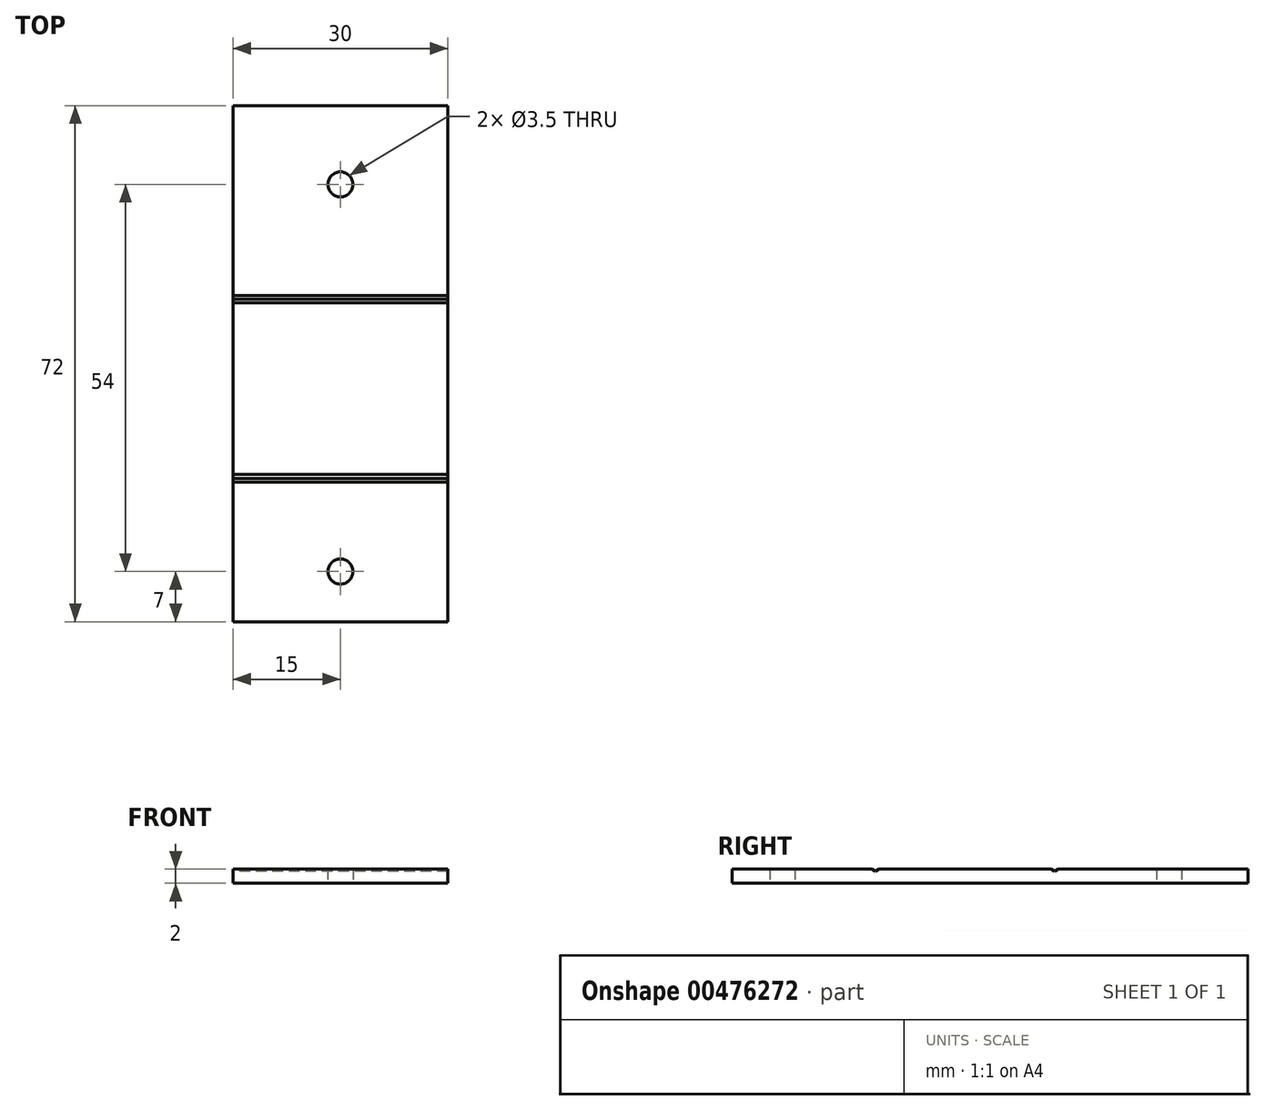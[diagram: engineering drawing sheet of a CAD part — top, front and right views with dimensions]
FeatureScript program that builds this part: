
annotation { "Feature Type Name" : "Feature", "Feature Type Description" : "" }
export const myFeature = defineFeature(function(context is Context, id is Id, definition is map)
    precondition{}
    {
        {
            var Q0;
            Q0=qCreatedBy(makeId("Top.planeOp"),FACE);
            var sketch = newSketch(context, id + "F0", { "sketchPlane" : qUnion([Q0])});
            skLineSegment(sketch, "E0.bottom", {"start": v(0, 0) * mm, "end": v(30, 0) * mm});
            skLineSegment(sketch, "E0.top", {"start": v(0, 72) * mm, "end": v(30, 72) * mm});
            skLineSegment(sketch, "E0.left", {"start": v(0, 0) * mm, "end": v(0, 72) * mm});
            skLineSegment(sketch, "E0.right", {"start": v(30, 0) * mm, "end": v(30, 72) * mm});
            skLineSegment(sketch, "E1", {"start": v(0, 45) * mm, "end": v(30, 45) * mm});
            skLineSegment(sketch, "E2", {"start": v(30, 20) * mm, "end": v(0, 20) * mm});
            skLineSegment(sketch, "E3", {"start": v(15, 72) * mm, "end": v(15, 0) * mm, "construction": true});
            skCircle(sketch, "E4", {"center": v(15, 61) * mm, "radius": 1.75 * mm});
            skCircle(sketch, "E5", {"center": v(15, 7) * mm, "radius": 1.75 * mm});
            skSolve(sketch);
        }
        {
            var Q0;
            {var subQ2=sQuery(id+"F0.wireOp",EDGE,"E0.top");Q0=makeQuery(id+"F0.imprint","IMPRINT",FACE,{"disambiguationData":[TD([[makeQuery(id+"F0.imprint","IMPRINT",EDGE,{"derivedFrom":subQ2}),-1.0]])]});}
            var Q1;
            {var subQ0=sQuery(id+"F0.wireOp",EDGE,"E1");Q1=makeQuery(id+"F0.imprint","IMPRINT",FACE,{"disambiguationData":[TD([[makeQuery(id+"F0.imprint","IMPRINT",EDGE,{"derivedFrom":subQ0}),-1.0]])]});}
            var Q2;
            {var subQ2=sQuery(id+"F0.wireOp",EDGE,"E0.bottom");Q2=makeQuery(id+"F0.imprint","IMPRINT",FACE,{"disambiguationData":[TD([[makeQuery(id+"F0.imprint","IMPRINT",EDGE,{"derivedFrom":subQ2}),1.0]])]});}
            extrude(context, id + "F1", {"entities" : qUnion([Q0, Q1, Q2]), "depth" : 2 * mm});
        }
        {
            var Q0;
            Q0=makeQuery(id+"F1.opExtrude","SWEPT_FACE",FACE,{"disambiguationData":[OSD([sQuery(id+"F0.wireOp",EDGE,"E0.left")])]});
            var sketch = newSketch(context, id + "F2", { "sketchPlane" : qUnion([Q0])});
            skLineSegment(sketch, "E6", {"start": v(-19.48, 2) * mm, "end": v(-20, 1.7) * mm});
            skLineSegment(sketch, "E7", {"start": v(-20, 1.7) * mm, "end": v(-20.52, 2) * mm});
            skLineSegment(sketch, "E8", {"start": v(-45.52, 2) * mm, "end": v(-45, 1.7) * mm});
            skLineSegment(sketch, "E9", {"start": v(-45, 1.7) * mm, "end": v(-44.48, 2) * mm});
            skLineSegment(sketch, "E10", {"start": v(-45.52, 2) * mm, "end": v(-44.48, 2) * mm});
            skLineSegment(sketch, "E11", {"start": v(-20.52, 2) * mm, "end": v(-19.48, 2) * mm});
            skSolve(sketch);
        }
        {
            var Q0;
            Q0 = qSketchRegion(id + "F2", true);
            extrude(context, id + "F3", {"entities" : qUnion([Q0]), "operationType" : NewBodyOperationType.REMOVE, "endBound" : BoundingType.THROUGH_ALL, "oppositeDirection" : true, "depth" : 25 * mm});
        }
    });
